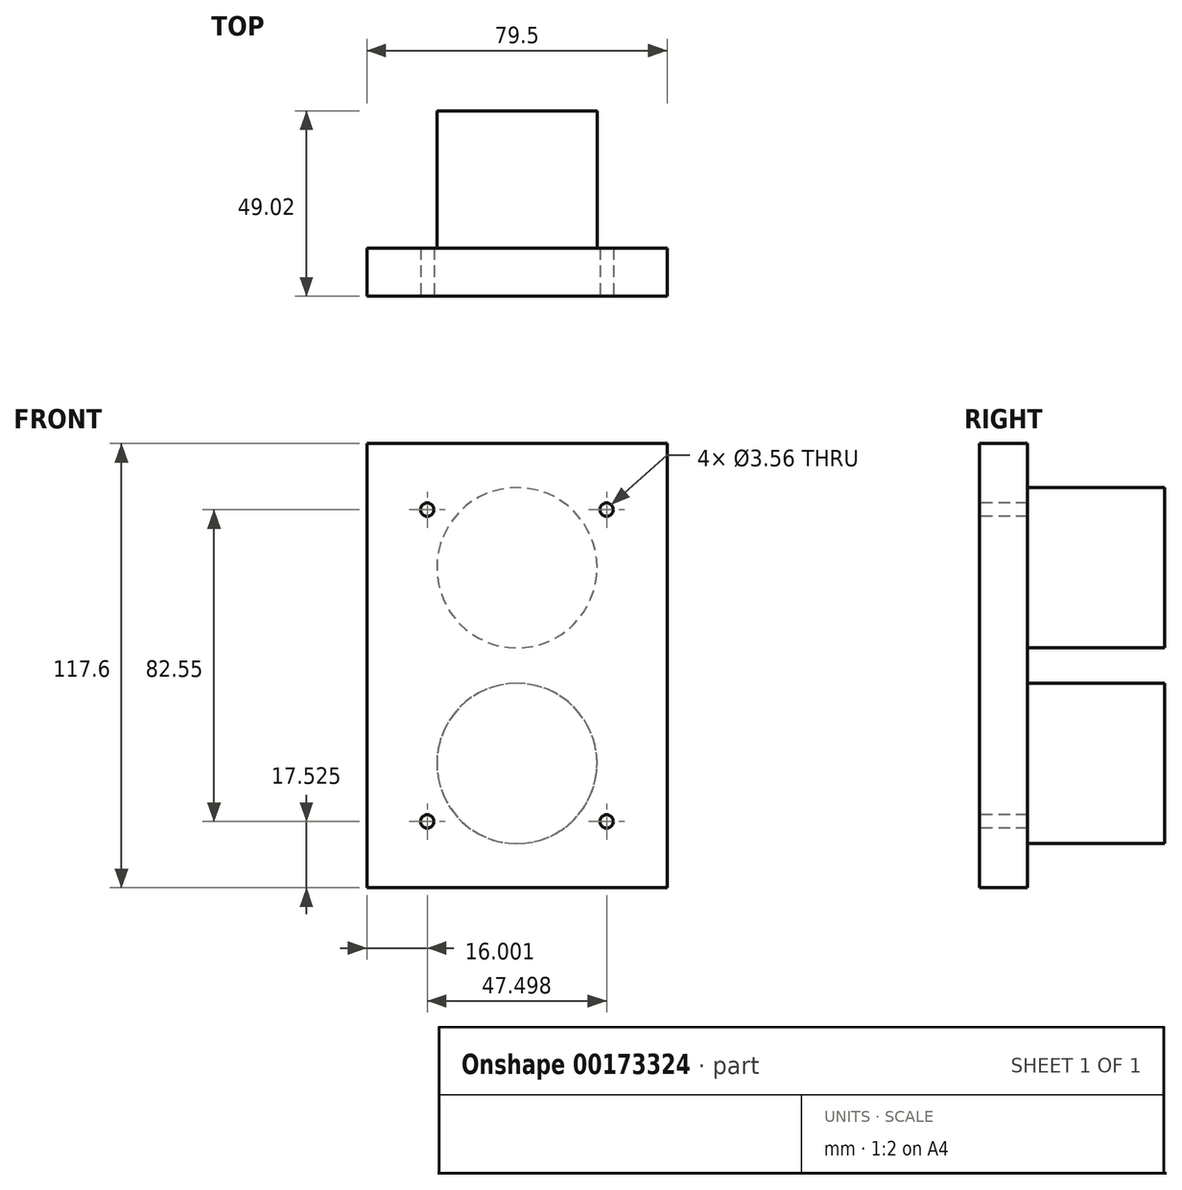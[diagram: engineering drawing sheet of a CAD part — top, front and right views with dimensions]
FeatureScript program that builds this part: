
annotation { "Feature Type Name" : "Feature", "Feature Type Description" : "" }
export const myFeature = defineFeature(function(context is Context, id is Id, definition is map)
    precondition{}
    {
        {
            var Q0;
            Q0=qCreatedBy(makeId("Front.planeOp"),FACE);
            var sketch = newSketch(context, id + "F0", { "sketchPlane" : qUnion([Q0])});
            skLineSegment(sketch, "E0.bottom", {"start": v(-39.75, 58.8) * mm, "end": v(39.75, 58.8) * mm});
            skLineSegment(sketch, "E0.top", {"start": v(-39.75, -58.8) * mm, "end": v(39.75, -58.8) * mm});
            skLineSegment(sketch, "E0.left", {"start": v(-39.75, 58.8) * mm, "end": v(-39.75, -58.8) * mm});
            skLineSegment(sketch, "E0.right", {"start": v(39.75, 58.8) * mm, "end": v(39.75, -58.8) * mm});
            skPoint(sketch, "E0.middle", {"position": v(0, 0) * mm});
            skSolve(sketch);
        }
        {
            var Q0;
            Q0 = qSketchRegion(id + "F0", true);
            extrude(context, id + "F1", {"entities" : qUnion([Q0]), "depth" : 12.7 * mm});
        }
        {
            var Q0;
            Q0=makeQuery(id+"F1.opExtrude","CAP_FACE",FACE,{"disambiguationData":[OSD([sQuery(id+"F0.wireOp",EDGE,"E0.bottom"),sQuery(id+"F0.wireOp",EDGE,"E0.top"),sQuery(id+"F0.wireOp",EDGE,"E0.left"),sQuery(id+"F0.wireOp",EDGE,"E0.right")])],"isStart":false});
            var sketch = newSketch(context, id + "F2", { "sketchPlane" : qUnion([Q0])});
            skCircle(sketch, "E1", {"center": v(-23.75, 41.28) * mm, "radius": 1.78 * mm});
            skCircle(sketch, "E2", {"center": v(23.75, 41.28) * mm, "radius": 1.78 * mm});
            skCircle(sketch, "E3", {"center": v(-23.75, -41.27) * mm, "radius": 1.78 * mm});
            skCircle(sketch, "E4", {"center": v(23.75, -41.27) * mm, "radius": 1.78 * mm});
            skLineSegment(sketch, "E5", {"start": v(0, 58.8) * mm, "end": v(0, -58.8) * mm});
            skSolve(sketch);
        }
        {
            var Q0;
            Q0 = qSketchRegion(id + "F2", true);
            extrude(context, id + "F3", {"entities" : qUnion([Q0]), "operationType" : NewBodyOperationType.REMOVE, "endBound" : BoundingType.THROUGH_ALL, "oppositeDirection" : true, "depth" : 25.4 * mm});
        }
        {
            var Q0;
            Q0=makeQuery(id+"F1.opExtrude","CAP_FACE",FACE,{"disambiguationData":[OSD([sQuery(id+"F0.wireOp",EDGE,"E0.bottom"),sQuery(id+"F0.wireOp",EDGE,"E0.top"),sQuery(id+"F0.wireOp",EDGE,"E0.left"),sQuery(id+"F0.wireOp",EDGE,"E0.right")])],"isStart":true});
            var sketch = newSketch(context, id + "F4", { "sketchPlane" : qUnion([Q0])});
            skCircle(sketch, "E6", {"center": v(0, 25.9) * mm, "radius": 21.2 * mm});
            skCircle(sketch, "E7", {"center": v(0, -25.9) * mm, "radius": 21.2 * mm});
            skSolve(sketch);
        }
        {
            var Q0;
            Q0 = qSketchRegion(id + "F4", true);
            extrude(context, id + "F5", {"entities" : qUnion([Q0]), "operationType" : NewBodyOperationType.ADD, "depth" : 36.32 * mm});
        }
    });
